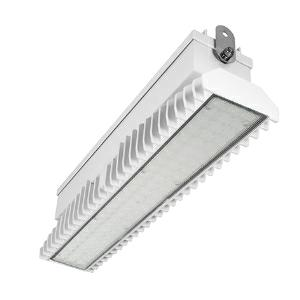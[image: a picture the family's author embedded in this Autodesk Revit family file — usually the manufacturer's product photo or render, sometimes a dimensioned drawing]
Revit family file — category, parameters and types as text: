
# Revit family: 3f_filippi_-_3f_lem_ampio_3f_filippi_-_59157_a0812_-_3f_lem_1_led_50-865_cr_ampio___vs_4861
name_source: partatom
category: Lighting Fixtures
units: mm (PartAtom-declared; Revit-internal decimal feet)

## family parameters
Cut with Voids When Loaded = No
Host = Face
Light Source = No
Part Type = Normal
Room Calculation Point = No
Round Connector Dimension = Use Diameter
Shared = No

## types (1)
- 3F Filippi - 3F LEM Ampio (1 x LED, 6652 lm, 56 W, 6500 K)
    Apparent Load = 56 VA
    Approval mark = CE
    CIE Flux Codes = 67 90 97 100 100
    Color Rendering = 80
    Color Temperature = 6500 K
    Control Gear = Electronic ballast
    Default Elevation = 1800 mm
    Description = Industrial luminaire with high light output and high luminous efficiency designed with the most innovative technologies for environments with temperature up to 55°C.

ILLUMINOTECHNICAL
Luminous efficiency 100% (DLOR 98%, ULOR 2%).
Initial luminous flux of the luminaire 6652 lm.
Direct symmetric wide distribution: the illuminated area has a rectangular shape.
Installation Interdistance Transv.D = 1.24 x hu - Long.D = 1.20 x hu.
Tabular UGR (CIE 117 - 4H-8H; S=0.25H; 70/50/20): RUG 25.9 - 25.7.
Beam angle: 82° - 83°.
Luminous efficacy 119 lm/W.
Lifetime (L93/B10): 30000 h. (tq+25°C)
Lifetime (L90/B10): 50000 h. (tq+25°C)
Lifetime (L85/B10): 80000 h. (tq+25°C)
Lifetime (L80/B10): 100000 h. (tq+25°C)
Lifetime (L85/B10): 50000 h. (tq+55°C)
Sudden decreased luminous flux after 50000 hours: 0% (C0).
Photobiological safety in compliance with IEC/TR 62778: RG0 risk exempt, (IEC 62471).
In compliance with IEC/EN 62722-2-1 - IEC/EN 62717 standards.

SOURCE
Mid-Power linear LED module 50W/865.
Energy efficiency class (UE 2019/2020 - UE 2019/2015): C.
CIE 13.3 Colour rendering index: CRI >80 (R9 <50%).
IES TM-30 Fidelity Index: Rf = 84 Rg = 95.
CCT nominal colour temperature 6500 K.
Colour initial tolerance (MacAdam): SDCM 3.

MECHANICAL
Passive modular heatsinks in die-casted aluminium, painted in white colour.
To optimize the thermal management of the LED module, the heatsinks are oversized and provided with self-cleaning of cooling fins.
Wiring body in aluminium and galvanised steel anchored solidly to the sinks and thermally separated.
3F Lens lenses with high luminous efficiency, transparent methacrylate (PMMA), fixed to the LED modules.
Fixing brackets in stainless steel.
Luminaire with limited surface temperature. - D - (EN 60598-2-24)
Dimensions: 542x115 mm, height 154 mm. Weight 7.225 kg.
IP65 protection degree.
Mechanical strength to impacts IK06 (1 joule).
Glow-wire test resistance 650°C.

ELECTRICAL
Halogen Free electronic wiring 230V-50/60Hz, power factor 0.95, THD <25%, constant output current, class I, 1 driver.
Power of the luminaire 56 W.
ENEC - CE.
SAFE FLICKER: PstLM=<1 and SVM=<0.4 (IEC TR 61547-1 and IEC TR 63158), to ensure a more comfortable and safe light.
Luminaire compliant with EN 60598-2-22 for power supply from a centralised emergency system CPSS (Central Power Supply System), not incorporated in the luminaire - high risk areas excluded. The default power and flux are 100% in AC and 100% in DC.
Ambient temperature from -30°C to +55°C.
Temperature class T6 max 85°C.
Quick connection via M20 3P connector with 9-13 mm tightening range.
Power unit positioned on a separate compartment by the LED module to ensure optimum temperatures of cabling components, to be inspectable and maintainable.
Relative humidity UR: <85%.

INSTALLATION
Ceiling / Suspended / Wall.
All accessories dedicated to this product are available on the Catalog and on our website www.3F-Filippi.com.

ACCESSORIES
A0812 - Anti-glare microprismatic VS moulded glass, tempered, not flammable, with sealing gasket.
One required for each light module. The pack contains 10 pieces.

APPLICATIONS
In commercial environments, exhibition and industrial areas, stores, open areas.
Applications with high ambient temperature up to 55°C.
Environments in which it is necessary a total protection against falling fragments (eg environments with foodstuffs or machines with moving parts or with extreme temperature changes), use luminaires with polycarbonate lenses.

WARNING
Fixture not suitable for cold stores with an ambient temperature <0°C and/or relative humidity >85%.
Luminaire designed for disposal/recycling at end-of-life.
Replaceable (LED only) light source by a professional. Replaceable control gear by a professional.
    Height = 154 mm
    Lamp = 1 x LED
    Lamp Light Flux = 6652 lm
    Lamp Power = 56 W
    Lamp count = 1
    Length = 542 mm
    Lifetime = 50000 h
    Luminous efficacy = 119 lm/W
    Manufacturer = 3F Filippi
    ModVariant = No
    Model = 3F Filippi - 59157+A0812 - 3F LEM 1 LED 50-865 CR AMPIO + VS
    Mounting Place = Ceiling
    Mounting Type = Pendant
    Number of Poles = 1
    OnlyDefault = Yes
    Power Factor = 1
    Product Name = 3F Filippi - 3F LEM Ampio
    Product group = pendant luminaire
    ProductGroupID = 9
    Protection Class = Protection class I
    Protection Degree = IP 65
    RLX_Detail_Level = 1
    RLX_Emergency_Light_Flux = 0 lm
    RLX_Emergency_Type = 0
    RLX_Emergency_Type_DB = No
    RlxData = <blob elided: 90485 chars, md5=7ed4aeb3>
    Socket = socket
    Standby Power = 0 W
    System Light Flux = 6652 lm
    System Power = 56 W
    Type Comments = Product without accessories
    Type Image = 3f_filippi_-_lem_1__a0812.jpg
    URL = http://relux.com
    VarID = ---
    Voltage = 0 V
    Weight = 0.00 kg
    Width = 115 mm

## geometry (parser evidence)
native form markers: Blend x4, Sweep x13
no freeform markers — native parametric forms only
